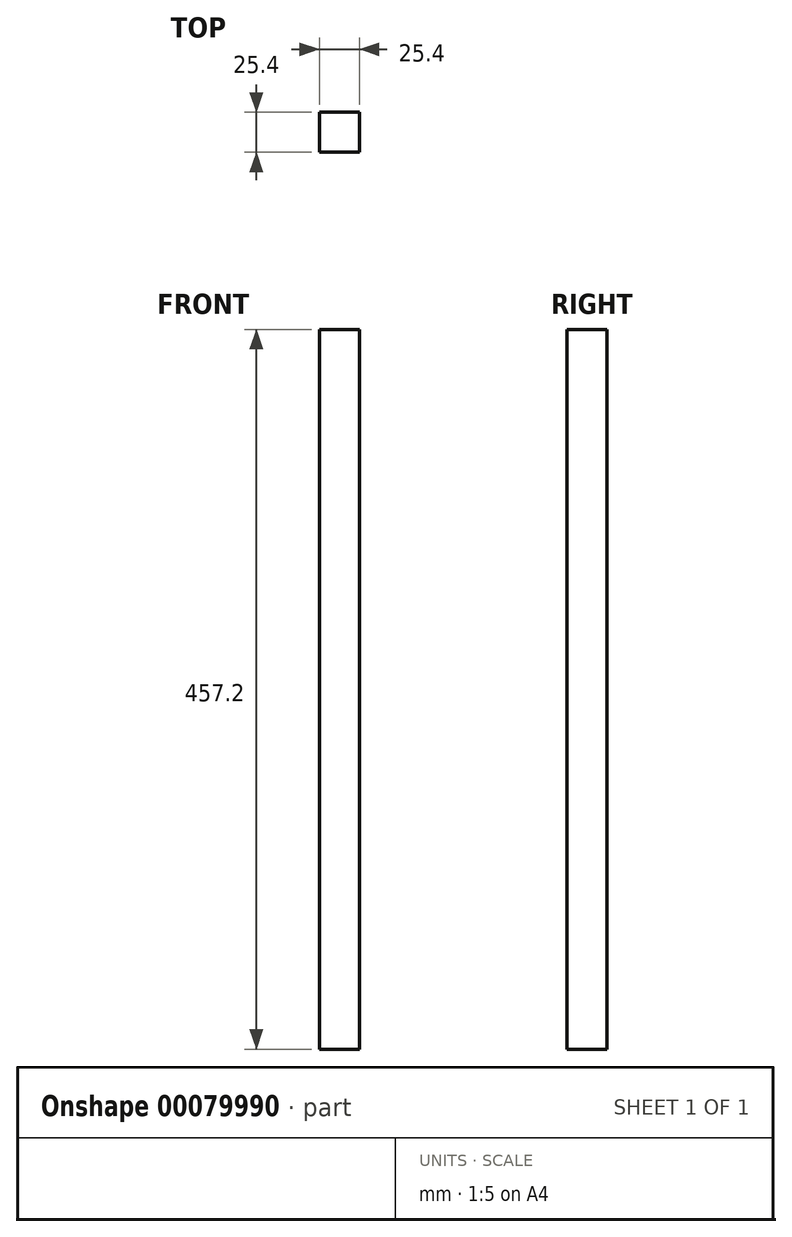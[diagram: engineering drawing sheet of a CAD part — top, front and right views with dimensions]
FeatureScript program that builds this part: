
annotation { "Feature Type Name" : "Feature", "Feature Type Description" : "" }
export const myFeature = defineFeature(function(context is Context, id is Id, definition is map)
    precondition{}
    {
        {
            var Q0;
            Q0=qCreatedBy(makeId("Top.planeOp"),FACE);
            var sketch = newSketch(context, id + "F0", { "sketchPlane" : qUnion([Q0])});
            skLineSegment(sketch, "E0.bottom", {"start": v(12.7, -12.7) * mm, "end": v(-12.7, -12.7) * mm});
            skLineSegment(sketch, "E0.top", {"start": v(12.7, 12.7) * mm, "end": v(-12.7, 12.7) * mm});
            skLineSegment(sketch, "E0.left", {"start": v(12.7, -12.7) * mm, "end": v(12.7, 12.7) * mm});
            skLineSegment(sketch, "E0.right", {"start": v(-12.7, -12.7) * mm, "end": v(-12.7, 12.7) * mm});
            skPoint(sketch, "E0.middle", {"position": v(0, 0) * mm});
            skSolve(sketch);
        }
        {
            var Q0;
            Q0=makeQuery(id+"F0.imprint","IMPRINT",FACE,{"disambiguationData":[TD([[makeQuery(id+"F0.imprint","IMPRINT",EDGE,{"derivedFrom":sQuery(id+"F0.wireOp",EDGE,"E0.bottom")}),-1.0]])]});
            extrude(context, id + "F1", {"entities" : qUnion([Q0]), "depth" : 457.2 * mm});
        }
    });
